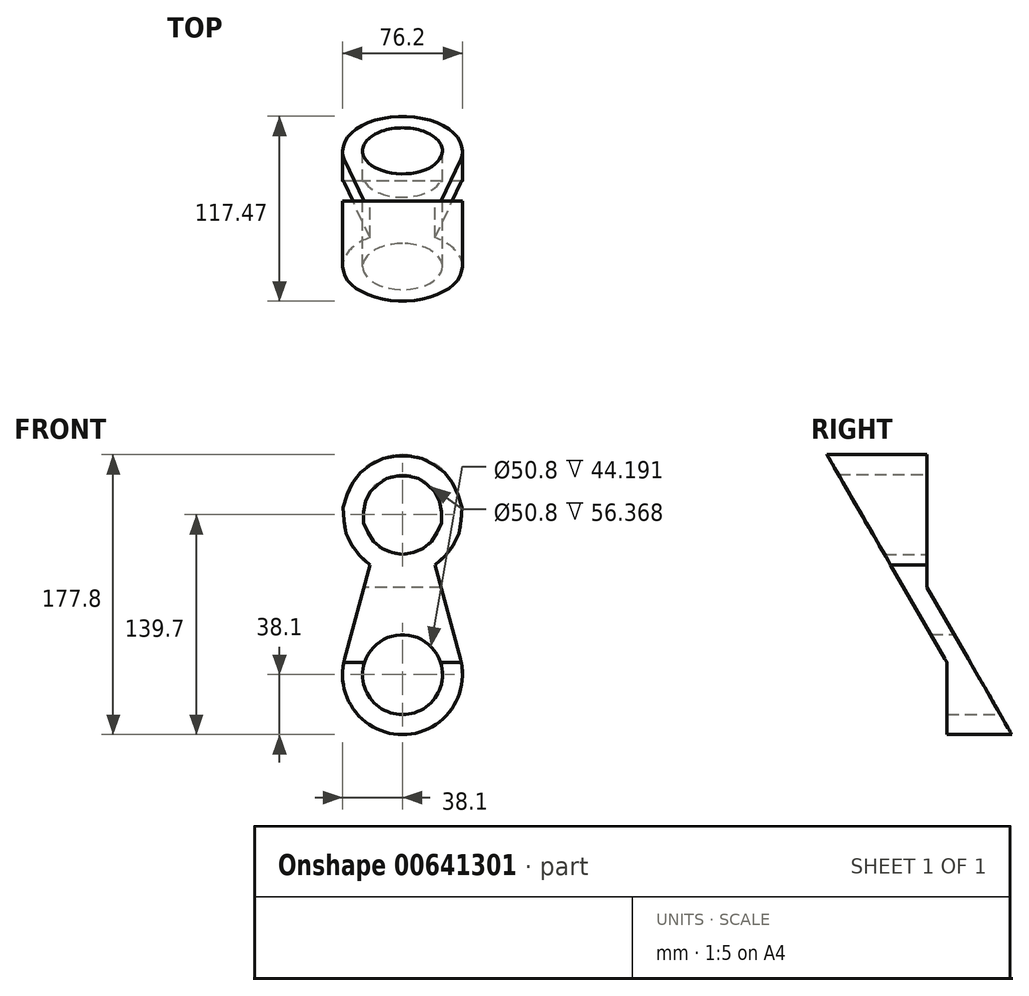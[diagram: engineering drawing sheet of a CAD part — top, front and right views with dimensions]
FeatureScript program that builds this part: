
annotation { "Feature Type Name" : "Feature", "Feature Type Description" : "" }
export const myFeature = defineFeature(function(context is Context, id is Id, definition is map)
    precondition{}
    {
        {
            var Q0;
            Q0=qCreatedBy(makeId("Front.planeOp"),FACE);
            var sketch = newSketch(context, id + "F0", { "sketchPlane" : qUnion([Q0])});
            skCircle(sketch, "E0", {"center": v(0, 50.8) * mm, "radius": 25.4 * mm});
            skCircle(sketch, "E1", {"center": v(0, -50.8) * mm, "radius": 25.4 * mm});
            skCircle(sketch, "E2", {"center": v(0, -50.8) * mm, "radius": 38.1 * mm});
            skCircle(sketch, "E3", {"center": v(0, 50.8) * mm, "radius": 38.1 * mm});
            skLineSegment(sketch, "E4", {"start": v(36.8, -40.94) * mm, "end": v(20.78, 18.86) * mm});
            skLineSegment(sketch, "E5", {"start": v(-36.8, -40.94) * mm, "end": v(-20.78, 18.86) * mm});
            skLineSegment(sketch, "E6", {"start": v(0, 50.8) * mm, "end": v(0, -50.8) * mm, "construction": true});
            skSolve(sketch);
        }
        {
            var Q0;
            Q0=makeQuery(id+"F0.imprint","IMPRINT",FACE,{"disambiguationData":[TD([[makeQuery(id+"F0.imprint","IMPRINT",EDGE,{"derivedFrom":sQuery(id+"F0.wireOp",EDGE,"E0")}),-1.0]])]});
            var Q1;
            {var subQ0=sQuery(id+"F0.wireOp",EDGE,"E4");Q1=makeQuery(id+"F0.imprint","IMPRINT",FACE,{"disambiguationData":[TD([[makeQuery(id+"F0.imprint","IMPRINT",EDGE,{"derivedFrom":subQ0}),1.0]])]});}
            var Q2;
            Q2=makeQuery(id+"F0.imprint","IMPRINT",FACE,{"disambiguationData":[TD([[makeQuery(id+"F0.imprint","IMPRINT",EDGE,{"derivedFrom":sQuery(id+"F0.wireOp",EDGE,"E1")}),-1.0]])]});
            extrude(context, id + "F1", {"entities" : qUnion([Q0, Q1, Q2]), "depth" : 63.5 * mm, "offsetDistance" : 25.4 * mm, "hasSecondDirection" : true, "secondDirectionOppositeDirection" : true, "secondDirectionDepth" : 53.97 * mm});
        }
        {
            var Q0;
            Q0=qCreatedBy(makeId("Right.planeOp"),FACE);
            var sketch = newSketch(context, id + "F2", { "sketchPlane" : qUnion([Q0])});
            skLineSegment(sketch, "E7.0", {"start": v(-63.5, 18.86) * mm, "end": v(-63.5, 88.9) * mm, "construction": true});
            skLineSegment(sketch, "E7.3.0", {"start": v(53.98, -40.94) * mm, "end": v(53.98, -88.9) * mm, "construction": true});
            skLineSegment(sketch, "E8.0", {"start": v(0, -88.9) * mm, "end": v(0, 88.9) * mm, "construction": true});
            skLineSegment(sketch, "E9.0", {"start": v(12.7, -88.9) * mm, "end": v(12.7, 88.9) * mm, "construction": true});
            skLineSegment(sketch, "E10", {"start": v(-63.5, 88.9) * mm, "end": v(12.7, -43.08) * mm});
            skLineSegment(sketch, "E11", {"start": v(53.98, -88.9) * mm, "end": v(0, 4.59) * mm});
            skPoint(sketch, "E12.orphan", {"position": v(53.97, -40.94) * mm});
            skLineSegment(sketch, "E13", {"start": v(0, 88.9) * mm, "end": v(-63.5, 88.9) * mm});
            skLineSegment(sketch, "E14", {"start": v(12.7, -43.08) * mm, "end": v(12.7, -88.9) * mm});
            skLineSegment(sketch, "E15", {"start": v(53.98, -88.9) * mm, "end": v(12.7, -88.9) * mm});
            skLineSegment(sketch, "E16", {"start": v(0, 4.59) * mm, "end": v(0, 88.9) * mm});
            skSolve(sketch);
        }
        {
            var Q0;
            Q0=makeQuery(id+"F2.imprint","IMPRINT",FACE,{"disambiguationData":[TD([[makeQuery(id+"F2.imprint","IMPRINT",EDGE,{"derivedFrom":sQuery(id+"F2.wireOp",EDGE,"E10")}),1.0]])]});
            extrude(context, id + "F3", {"entities" : qUnion([Q0]), "operationType" : NewBodyOperationType.INTERSECT, "endBound" : BoundingType.SYMMETRIC, "depth" : 101.6 * mm, "offsetDistance" : 25.4 * mm});
        }
    });
